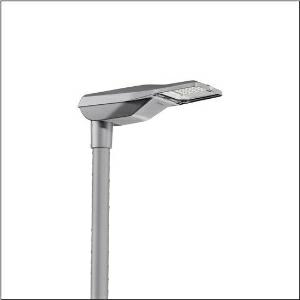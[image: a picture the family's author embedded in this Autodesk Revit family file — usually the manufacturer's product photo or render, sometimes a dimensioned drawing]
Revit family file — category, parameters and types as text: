
# Revit family: streetlight_sl_21_iq_micro___st1_5a_5xe1p31d08cb_2d79
name_source: partatom
category: Lighting Fixtures
units: mm (PartAtom-declared; Revit-internal decimal feet)

## family parameters
Cut with Voids When Loaded = No
Host = Face
Light Source = No
Part Type = Normal
Room Calculation Point = No
Round Connector Dimension = Use Diameter
Shared = No

## types (1)
- --- (1 x LED, 2820 lm, 19.4 W, 3000K)
    Apparent Load = 19 VA
    CIE Flux Codes = 22 53 95 100 100
    Color Rendering = 70
    Color Temperature = 3000K
    Default Elevation = 1800 mm
    Description = Streetlight SL 21 iQ micro, mast luminaire, primary light control with lens, of PMMA, primary optical cover: cover, of toughened safety glass, transparent, light distribution: ST1.5a, light emission: direct distribution, primary light characteristic: asymmetric, installation type: post-top, side-entry, LED, High Power LED, rated luminous flux: 2.820lm, luminous efficacy: 145lm/W, light colour: 730, colour temperature: 3000K, control gear: iQ-Comfort, control: Auto-Match, Temp-Guard, Lumen-Switch, Night-Set, Smart-Wire, Light-Fading, Desk-Remote (wireless, voltage-free reading and setting of iQ features in the workshop via application-optimized NFC function/RFID function), optimised constant luminous flux control (CLO 2.0), pre-setting: linear dimming characteristic, mains connection: 220..240V, AC, 50/60Hz, start of lifetime: 19W, end of service life: 20W, reduction: 10W, luminaire housing, of diecast aluminium, powder-coated, SITECO metallic grey (DB 702S), corrosivity category C5 high according to DIN EN ISO 12944, please order mast flange separately, inclination adjustable: 0°, 5°, 10°, 15°, sealing non-destructively replaceable, multi-level sealing system, length: 528mm, width: 235mm, height: 110mm, mast flange for spigot size: 42mm (side-entry): 5XC10008XM4, 60/48mm (side-entry/post-top): 5XC10108XM2, 76/60mm (side-entry/post-top): 5XC10108XM1, protection rating (complete): IP66, insulation class (complete): insulation class II (safety insulation), certification: CE, ENEC, ENEC+, VDE, impact resistance: IK10, permissible operating ambient temperature for outdoor applications: -40..+50°C, standard-compliant lighting for roads and squares, packaging unit: 1 piece

Light Distribution: ST1.5a
    Height = 110 mm
    Lamp = 1 x LED
    Lamp Light Flux = 2820 lm
    Lamp Power = 19.4 W
    Lamp count = 1
    Length = 528 mm
    Luminous efficacy = 145 lm/W
    Manufacturer = Siteco
    ModVariant = No
    Model = 5XE1P31D08CB
    Number of Poles = 1
    OnlyDefault = Yes
    Power Factor = 1
    Product Name = Streetlight SL 21 iQ micro | ST1.5a
    Product group = mast luminaire | pylon top
    ProductGroupID = 6100
    Protection Class = Protection class II
    Protection Degree = IP 66
    RLX_Detail_Level = 1
    RLX_Emergency_Light_Flux = 0 lm
    RLX_Emergency_Type = 0
    RLX_Emergency_Type_DB = No
    RlxData = <blob elided: 102941 chars, md5=4c094648>
    Socket = socket
    Standby Power = 0 W
    System Light Flux = 2820 lm
    System Power = 19 W
    Type Comments = factory setting: luminous flux: 100 % | dim-lin: 254 | 387 mA
    Type Image = l_1006881.jpg
    URL = http://relux.com
    VarID = @adj_137603
    Voltage = 0 V
    Weight = 0.00 kg
    Width = 235 mm

## geometry (parser evidence)
native form markers: Blend x4, Sweep x8
no freeform markers — native parametric forms only
